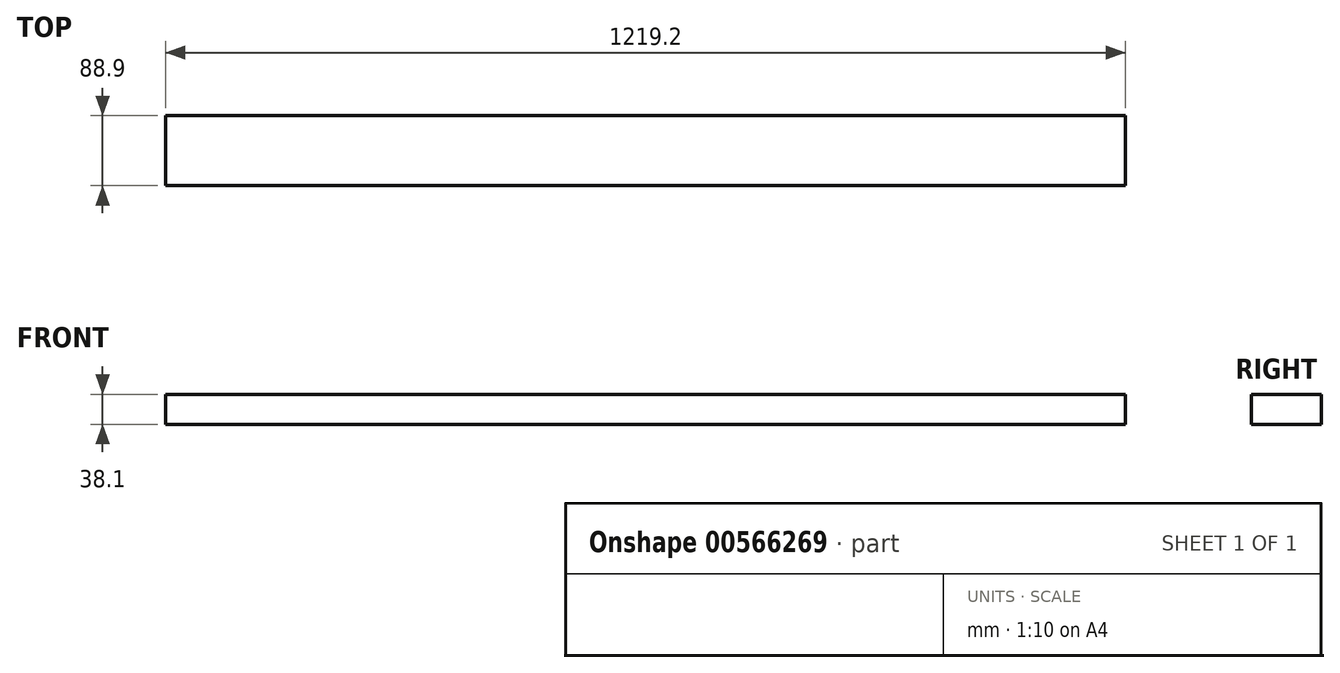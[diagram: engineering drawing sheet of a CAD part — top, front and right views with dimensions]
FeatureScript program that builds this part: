
annotation { "Feature Type Name" : "Feature", "Feature Type Description" : "" }
export const myFeature = defineFeature(function(context is Context, id is Id, definition is map)
    precondition{}
    {
        {
            var Q0;
            Q0=qCreatedBy(makeId("Front.planeOp"),FACE);
            var sketch = newSketch(context, id + "F0", { "sketchPlane" : qUnion([Q0])});
            skLineSegment(sketch, "E0.bottom", {"start": v(-609.6, 19.05) * mm, "end": v(609.6, 19.05) * mm});
            skLineSegment(sketch, "E0.top", {"start": v(-609.6, -19.05) * mm, "end": v(609.6, -19.05) * mm});
            skLineSegment(sketch, "E0.left", {"start": v(-609.6, 19.05) * mm, "end": v(-609.6, -19.05) * mm});
            skLineSegment(sketch, "E0.right", {"start": v(609.6, 19.05) * mm, "end": v(609.6, -19.05) * mm});
            skPoint(sketch, "E0.middle", {"position": v(0, 0) * mm});
            skSolve(sketch);
        }
        {
            var Q0;
            Q0=makeQuery(id+"F0.imprint","IMPRINT",FACE,{"disambiguationData":[TD([[makeQuery(id+"F0.imprint","IMPRINT",EDGE,{"derivedFrom":sQuery(id+"F0.wireOp",EDGE,"E0.bottom")}),-1.0]])]});
            extrude(context, id + "F1", {"entities" : qUnion([Q0]), "depth" : 88.9 * mm, "offsetDistance" : 25.4 * mm});
        }
    });
